# Revit family: VHS-DV_Straight_DN15-DN20_RFA_2
name_source: partatom
category: Pipe Accessories
units: mm (PartAtom-declared; Revit-internal decimal feet)

## family parameters
Always vertical = Yes
Cut with Voids When Loaded = No
OmniClass Number = 23.65.55.14.17
OmniClass Title = Adjusting/Controlling Valves for Liquid Services
Part Type = Valve - Breaks Into
Round Connector Dimension = Use Diameter
Shared = No
Work Plane-Based = No

## types (3) — shared parameters
Application = 2-pipe system
CC_2 = 25 mm  [stored 0.082021 ft]
CGAP = 50 mm  [stored 0.164042 ft]
CenSd_R22_6 = 5 mm  [stored 0.0164042 ft]
CenSd_R5_6 = 15 mm  [stored 0.0492126 ft]
DS = 20 mm
Description = Thermostatic H-piece Valve
H0 = 29 mm
H2 = 7 mm  [stored 0.0229659 ft]
H3 = 4 mm  [stored 0.0131234 ft]
H4 = 3 mm  [stored 0.00984252 ft]
H5 = 3 mm  [stored 0.00984252 ft]
H6 = 4 mm  [stored 0.0131234 ft]
H7 = 5 mm  [stored 0.0164042 ft]
IfcExportAs = IfcValveType
IfcExportType = VHS-DV_Straight
L = 138 mm
L1 = 8 mm  [stored 0.0262467 ft]
L10 = 2 mm  [stored 0.00656168 ft]
L11 = 2 mm  [stored 0.00656168 ft]
L11__ve = -2 mm  [stored -0.00656168 ft]
L12 = 6 mm  [stored 0.019685 ft]
L12__ve = -6 mm  [stored -0.019685 ft]
L13 = 3 mm  [stored 0.00984252 ft]
L14 = 3 mm  [stored 0.00984252 ft]
L14__ve = -3 mm  [stored -0.00984252 ft]
L15 = 4 mm  [stored 0.0131234 ft]
L15__ve = -4 mm  [stored -0.0131234 ft]
L16 = 36 mm  [stored 0.11811 ft]
L1__ve = -8 mm  [stored -0.0262467 ft]
L2 = 72 mm  [stored 0.23622 ft]
L2D_Min = 3048 mm
L3 = 10 mm  [stored 0.0328084 ft]
L4 = 16 mm  [stored 0.0524934 ft]
L4_2 = 8 mm  [stored 0.0262467 ft]
L5 = 6 mm  [stored 0.019685 ft]
L6 = 2 mm  [stored 0.00656168 ft]
L6__ve = -2 mm  [stored -0.00656168 ft]
L7 = 6 mm  [stored 0.019685 ft]
L7__ve = -6 mm  [stored -0.019685 ft]
L8 = 2 mm  [stored 0.00656168 ft]
L9 = 2 mm  [stored 0.00656168 ft]
L9__ve = -2 mm  [stored -0.00656168 ft]
LC = 54 mm  [stored 0.177165 ft]
LOD 200 = No
LOD 350 = Yes
L_EQ = 25 mm  [stored 0.082021 ft]
Manufacturer = Danfoss
Max Differential Pressure = 0.6 bar
Max Flow (Text) = 135 l/h
Max Operating Pressure = 10 bar
Max Working Temperature = 95° C
Min Differential Pressure = 0.1 bar
Min Working Temperature = 2° C
NL1 = 8 mm  [stored 0.0262467 ft]
NL2 = 10 mm  [stored 0.0328084 ft]
R1 = 11 mm  [stored 0.0360892 ft]
R10 = 12 mm  [stored 0.0393701 ft]
R11 = 12 mm  [stored 0.0393701 ft]
R12 = 11 mm  [stored 0.0360892 ft]
R13 = 14 mm  [stored 0.0459318 ft]
R14 = 11 mm  [stored 0.0360892 ft]
R15 = 10 mm  [stored 0.0328084 ft]
R16 = 9 mm  [stored 0.0295276 ft]
R17 = 8 mm  [stored 0.0262467 ft]
R18 = 10 mm  [stored 0.0328084 ft]
R18_1 = 10 mm  [stored 0.0328084 ft]
R18_2 = 9 mm  [stored 0.0295276 ft]
R19 = 9 mm  [stored 0.0295276 ft]
R2 = 12 mm  [stored 0.0393701 ft]
R20 = 10 mm  [stored 0.0328084 ft]
R21 = 8 mm  [stored 0.0262467 ft]
R22 = 6 mm  [stored 0.019685 ft]
R23 = 1 mm  [stored 0.00328084 ft]
R24 = 13 mm
R25 = 12 mm  [stored 0.0393701 ft]
R26 = 9 mm  [stored 0.0295276 ft]
R3 = 10 mm  [stored 0.0328084 ft]
R4 = 15 mm  [stored 0.0492126 ft]
R5 = 17 mm
R7 = 15 mm  [stored 0.0492126 ft]
R8 = 11 mm  [stored 0.0360892 ft]
R9 = 9 mm  [stored 0.0295276 ft]
RN = 13 mm
RS = 10 mm  [stored 0.0328084 ft]
Setting Range = 1-7,N
TD = 34 mm
TL1 = 76 mm
TL2 = 62 mm  [stored 0.203412 ft]
URL = https://store.danfoss.com
Valve Body Material = Danfoss Brass (Nickel plated)
W = 34 mm
zero-valued in all types: L2D

## per-type parameters (varying)
| type | BBH | DR | H | H1 | HH | Model | Model Type | R | R6 | V1 | W2D | Weight |
| VHS-DV_Straight_Normal Flow_DN15-DN20_013G7876 | 52 mm  [stored 0.170604 ft] | 15 mm | 81 mm  [stored 0.265748 ft] | 41 mm  [stored 0.134514 ft] | 39 mm  [stored 0.127953 ft] | 013G7876 | VHS-DV_Straight_Normal Flow_DN15-DN20 | 8 mm  [stored 0.0262467 ft] | 12 mm  [stored 0.0393701 ft] | Yes | 15 mm  [stored 0.0492126 ft] | 0.56 kg |
| VHS-DV_Straight_Normal Flow_DN20-DN20_013G7879 | 40 mm  [stored 0.131234 ft] | 20 mm | 69 mm | 40 mm  [stored 0.131234 ft] | 38 mm | 013G7879 | VHS-DV_Straight_Normal Flow_DN20-DN20 | 10 mm  [stored 0.0328084 ft] | 11 mm  [stored 0.0360892 ft] | No | 20 mm  [stored 0.0656168 ft] | 0.50 kg |
| VHS-DV_Straight_Return Flow_DN15-DN20_013G7915 | 52 mm  [stored 0.170604 ft] | 15 mm | 81 mm  [stored 0.265748 ft] | 41 mm  [stored 0.134514 ft] | 39 mm  [stored 0.127953 ft] | 013G7915 | VHS-DV_Straight_Return Flow_DN15-DN20 | 8 mm  [stored 0.0262467 ft] | 12 mm  [stored 0.0393701 ft] | Yes | 15 mm  [stored 0.0492126 ft] | 0.56 kg |

note: [stored X ft] marks values corroborated as IEEE doubles in the binary element streams (Revit-internal decimal feet)

## geometry (parser evidence)
native form markers: Sweep x20
no freeform markers — native parametric forms only
